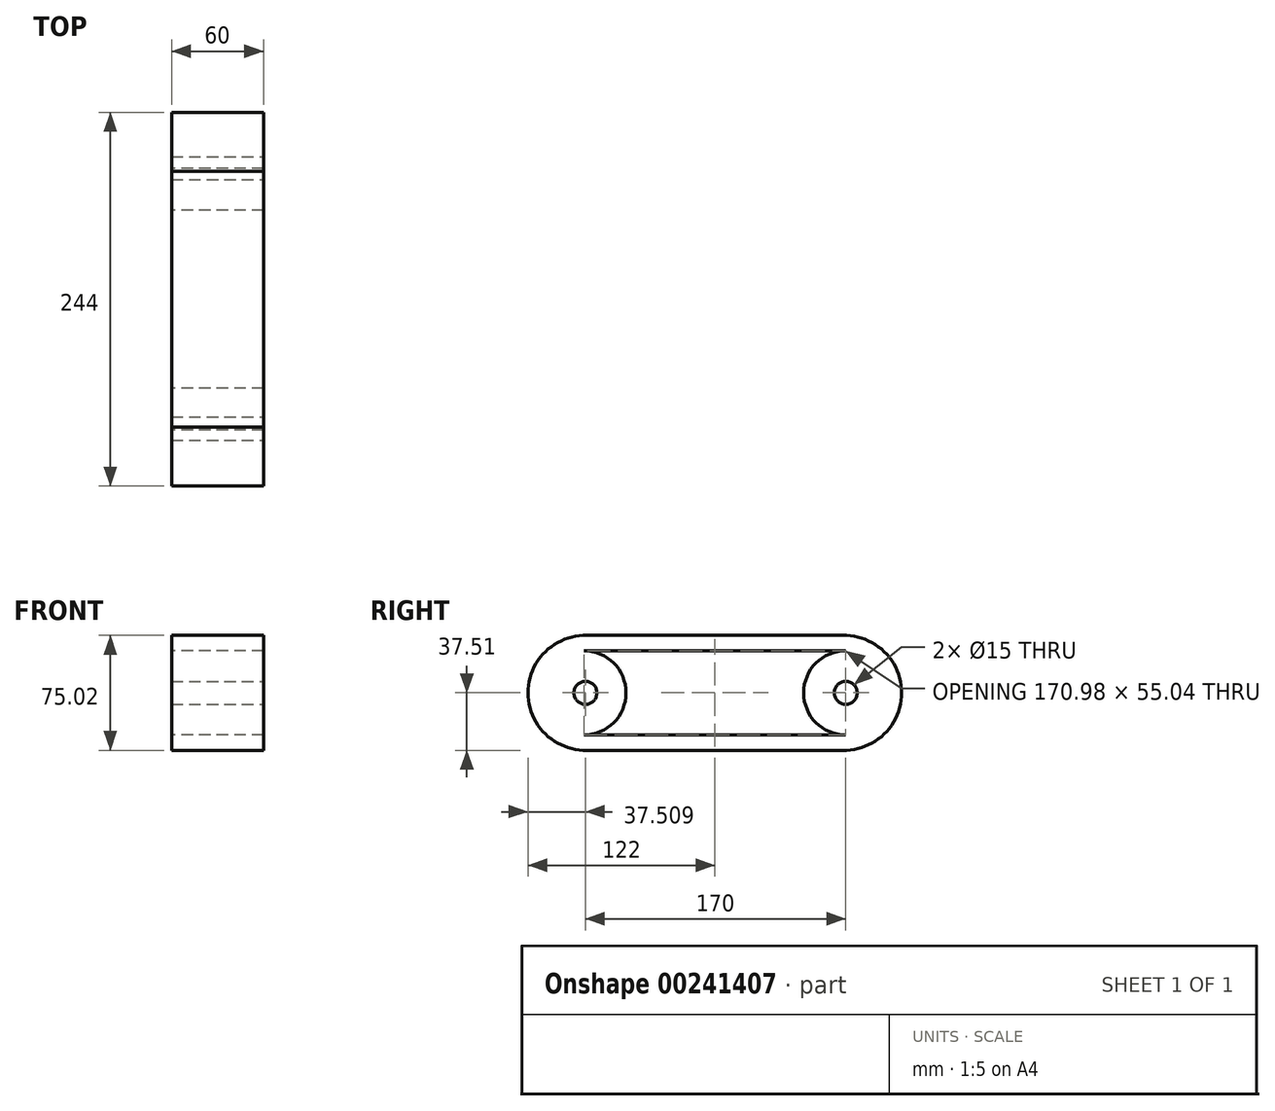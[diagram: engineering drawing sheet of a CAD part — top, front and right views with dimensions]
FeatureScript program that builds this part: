
annotation { "Feature Type Name" : "Feature", "Feature Type Description" : "" }
export const myFeature = defineFeature(function(context is Context, id is Id, definition is map)
    precondition{}
    {
        {
            var Q0;
            Q0=qCreatedBy(makeId("Right.planeOp"),FACE);
            var sketch = newSketch(context, id + "F0", { "sketchPlane" : qUnion([Q0])});
            skLineSegment(sketch, "E0.bottom", {"start": v(-83.5, 37.5) * mm, "end": v(83.5, 37.5) * mm});
            skLineSegment(sketch, "E0.top", {"start": v(-83.5, -37.5) * mm, "end": v(83.5, -37.5) * mm});
            skLineSegment(sketch, "E0.left", {"start": v(-83.5, 37.5) * mm, "end": v(-83.5, -37.5) * mm});
            skLineSegment(sketch, "E0.right", {"start": v(83.5, 37.5) * mm, "end": v(83.5, -37.5) * mm});
            skPoint(sketch, "E0.middle", {"position": v(0, 0) * mm});
            skLineSegment(sketch, "E1.bottom", {"start": v(-83.5, 27.5) * mm, "end": v(83.5, 27.5) * mm});
            skLineSegment(sketch, "E1.top", {"start": v(-83.5, -27.5) * mm, "end": v(83.5, -27.5) * mm});
            skLineSegment(sketch, "E1.left", {"start": v(-83.5, 27.5) * mm, "end": v(-83.5, -27.5) * mm});
            skLineSegment(sketch, "E1.right", {"start": v(83.5, 27.5) * mm, "end": v(83.5, -27.5) * mm});
            skArc(sketch, "E2", {"start": v(-83.5, 37.5) * mm, "mid": v(-122, 0) * mm, "end": v(-83.5, -37.5) * mm});
            skArc(sketch, "E3", {"start": v(83.5, -37.5) * mm, "mid": v(122, 0) * mm, "end": v(83.5, 37.5) * mm});
            skArc(sketch, "E4", {"start": v(-83.5, 27.5) * mm, "mid": v(-112, 0) * mm, "end": v(-83.5, -27.5) * mm});
            skArc(sketch, "E5", {"start": v(83.5, -27.5) * mm, "mid": v(112, 0) * mm, "end": v(83.5, 27.5) * mm});
            skSolve(sketch);
        }
        {
            var Q0;
            {var subQ0=sQuery(id+"F0.wireOp",EDGE,"E0.bottom");Q0=makeQuery(id+"F0.imprint","IMPRINT",FACE,{"disambiguationData":[TD([[makeQuery(id+"F0.imprint","IMPRINT",EDGE,{"derivedFrom":subQ0}),-1.0]])]});}
            var Q1;
            {var subQ0=sQuery(id+"F0.wireOp",EDGE,"E2");Q1=makeQuery(id+"F0.imprint","IMPRINT",FACE,{"disambiguationData":[TD([[makeQuery(id+"F0.imprint","IMPRINT",EDGE,{"derivedFrom":subQ0}),1.0]])]});}
            var Q2;
            {var subQ0=sQuery(id+"F0.wireOp",EDGE,"E0.top");Q2=makeQuery(id+"F0.imprint","IMPRINT",FACE,{"disambiguationData":[TD([[makeQuery(id+"F0.imprint","IMPRINT",EDGE,{"derivedFrom":subQ0}),1.0]])]});}
            var Q3;
            {var subQ0=sQuery(id+"F0.wireOp",EDGE,"E3");Q3=makeQuery(id+"F0.imprint","IMPRINT",FACE,{"disambiguationData":[TD([[makeQuery(id+"F0.imprint","IMPRINT",EDGE,{"derivedFrom":subQ0}),1.0]])]});}
            extrude(context, id + "F1", {"entities" : qUnion([Q0, Q1, Q2, Q3]), "depth" : 60 * mm});
        }
        {
            var Q0;
            Q0=qCreatedBy(makeId("Right.planeOp"),FACE);
            var sketch = newSketch(context, id + "F2", { "sketchPlane" : qUnion([Q0])});
            skCircle(sketch, "E6", {"center": v(-85.5, 0) * mm, "radius": 27.5 * mm});
            skCircle(sketch, "E7", {"center": v(85.5, 0) * mm, "radius": 27.5 * mm});
            skSolve(sketch);
        }
        {
            var Q0;
            Q0 = qSketchRegion(id + "F2", true);
            extrude(context, id + "F3", {"entities" : qUnion([Q0]), "operationType" : NewBodyOperationType.ADD, "depth" : 60 * mm});
        }
        {
            var Q0;
            Q0=makeQuery(id+"F3.opExtrude","CAP_FACE",FACE,{"disambiguationData":[OSD([sQuery(id+"F2.wireOp",EDGE,"E6")])],"isStart":false});
            var sketch = newSketch(context, id + "F4", { "sketchPlane" : qUnion([Q0])});
            skCircle(sketch, "E8", {"center": v(-84.5, 0) * mm, "radius": 7.5 * mm});
            skSolve(sketch);
        }
        {
            var Q0;
            Q0=makeQuery(id+"F3.opExtrude","CAP_FACE",FACE,{"disambiguationData":[OSD([sQuery(id+"F2.wireOp",EDGE,"E7")])],"isStart":false});
            var sketch = newSketch(context, id + "F5", { "sketchPlane" : qUnion([Q0])});
            skCircle(sketch, "E9", {"center": v(85.5, 0) * mm, "radius": 7.5 * mm});
            skSolve(sketch);
        }
        {
            var Q0;
            Q0 = qSketchRegion(id + "F5", true);
            var Q1;
            Q1 = qSketchRegion(id + "F4", true);
            extrude(context, id + "F6", {"entities" : qUnion([Q0, Q1]), "operationType" : NewBodyOperationType.REMOVE, "endBound" : BoundingType.THROUGH_ALL, "oppositeDirection" : true, "depth" : 25 * mm});
        }
    });
